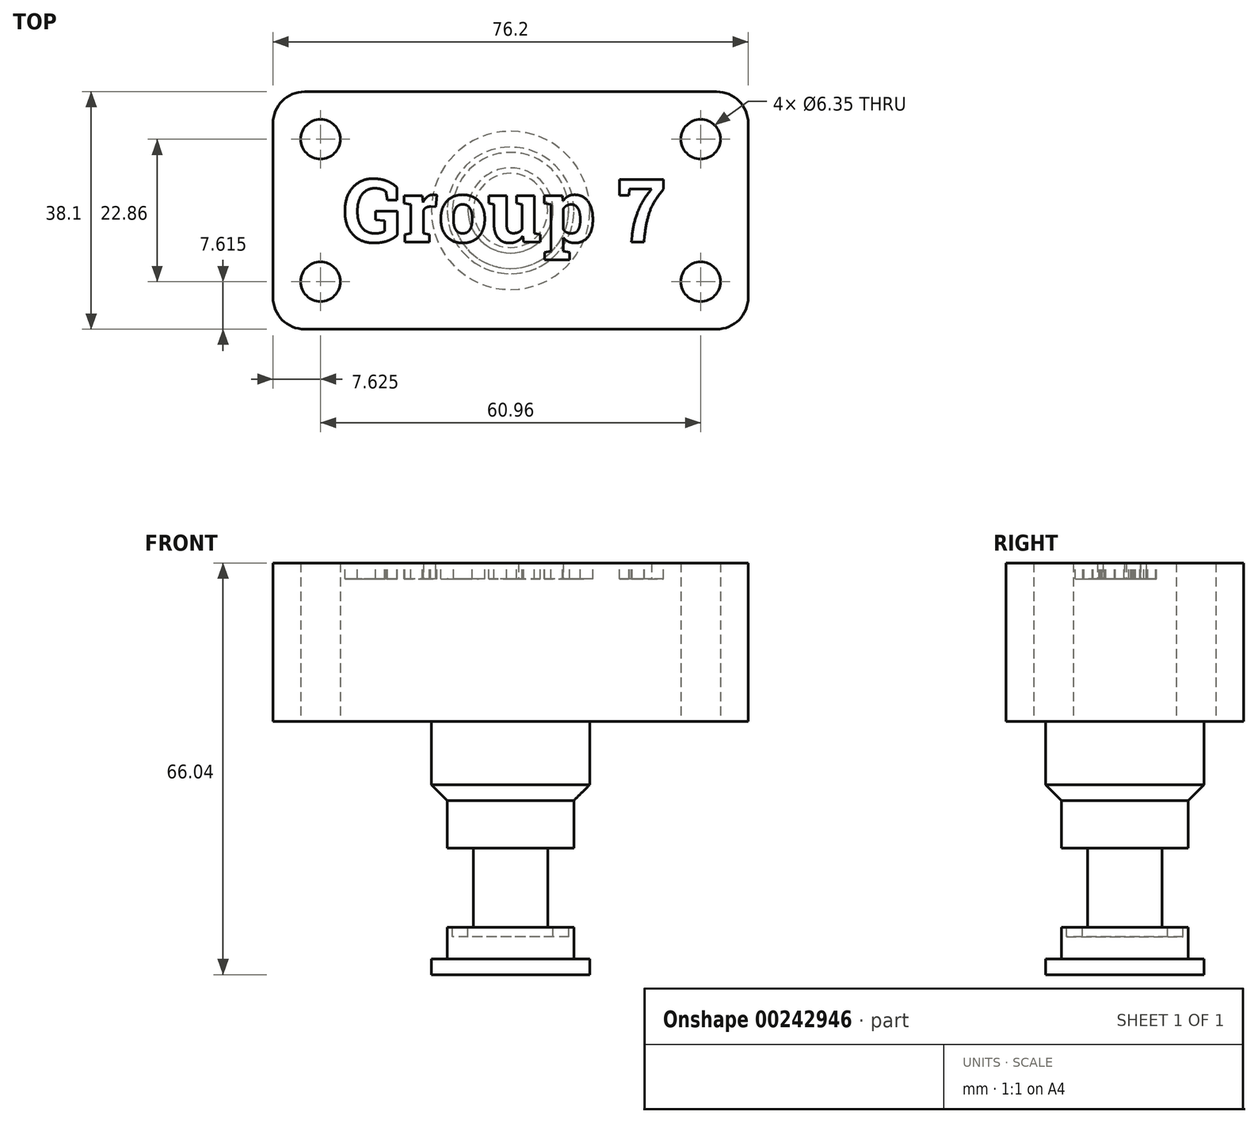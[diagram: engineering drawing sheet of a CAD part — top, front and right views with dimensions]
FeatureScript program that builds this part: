
annotation { "Feature Type Name" : "Feature", "Feature Type Description" : "" }
export const myFeature = defineFeature(function(context is Context, id is Id, definition is map)
    precondition{}
    {
        {
            var Q0;
            Q0=qCreatedBy(makeId("Top.planeOp"),FACE);
            var sketch = newSketch(context, id + "F0", { "sketchPlane" : qUnion([Q0])});
            skLineSegment(sketch, "E0.bottom", {"start": v(-28.39, 17.4) * mm, "end": v(47.81, 17.4) * mm});
            skLineSegment(sketch, "E0.top", {"start": v(-28.39, -20.7) * mm, "end": v(47.81, -20.7) * mm});
            skLineSegment(sketch, "E0.left", {"start": v(-28.39, 17.4) * mm, "end": v(-28.39, -20.7) * mm});
            skLineSegment(sketch, "E0.right", {"start": v(47.81, 17.4) * mm, "end": v(47.81, -20.7) * mm});
            skSolve(sketch);
        }
        {
            var Q0;
            Q0 = qSketchRegion(id + "F0", true);
            extrude(context, id + "F1", {"entities" : qUnion([Q0]), "depth" : 25.4 * mm});
        }
        {
            var Q0;
            Q0=makeQuery(id+"F1.opExtrude","SWEPT_EDGE",EDGE,{"disambiguationData":[OSD([sQuery(id+"F0.wireOp",EDGE,"E0.bottom"),sQuery(id+"F0.wireOp",EDGE,"E0.right")])]});
            var Q1;
            Q1=makeQuery(id+"F1.opExtrude","SWEPT_EDGE",EDGE,{"disambiguationData":[OSD([sQuery(id+"F0.wireOp",EDGE,"E0.top"),sQuery(id+"F0.wireOp",EDGE,"E0.right")])]});
            var Q2;
            Q2=makeQuery(id+"F1.opExtrude","SWEPT_EDGE",EDGE,{"disambiguationData":[OSD([sQuery(id+"F0.wireOp",EDGE,"E0.bottom"),sQuery(id+"F0.wireOp",EDGE,"E0.left")])]});
            var Q3;
            Q3=makeQuery(id+"F1.opExtrude","SWEPT_EDGE",EDGE,{"disambiguationData":[OSD([sQuery(id+"F0.wireOp",EDGE,"E0.top"),sQuery(id+"F0.wireOp",EDGE,"E0.left")])]});
            fillet(context, id + "F2", {"entities" : qUnion([Q0, Q1, Q2, Q3]), "radius" : 5.08 * mm, "tangentPropagation" : true, "allowEdgeOverflow" : false});
        }
        {
            var Q0;
            Q0=qCreatedBy(makeId("Top.planeOp"),FACE);
            var sketch = newSketch(context, id + "F3", { "sketchPlane" : qUnion([Q0])});
            skCircle(sketch, "E1", {"center": v(-20.77, 9.78) * mm, "radius": 3.18 * mm});
            skSolve(sketch);
        }
        {
            var Q0;
            Q0=qCreatedBy(makeId("Top.planeOp"),FACE);
            var sketch = newSketch(context, id + "F4", { "sketchPlane" : qUnion([Q0])});
            skCircle(sketch, "E2", {"center": v(40.2, 9.78) * mm, "radius": 3.18 * mm});
            skSolve(sketch);
        }
        {
            var Q0;
            Q0=qCreatedBy(makeId("Top.planeOp"),FACE);
            var sketch = newSketch(context, id + "F5", { "sketchPlane" : qUnion([Q0])});
            skCircle(sketch, "E3", {"center": v(-20.77, -13.08) * mm, "radius": 3.18 * mm});
            skSolve(sketch);
        }
        {
            var Q0;
            Q0=qCreatedBy(makeId("Top.planeOp"),FACE);
            var sketch = newSketch(context, id + "F6", { "sketchPlane" : qUnion([Q0])});
            skCircle(sketch, "E4", {"center": v(40.2, -13.08) * mm, "radius": 3.18 * mm});
            skSolve(sketch);
        }
        {
            var Q0;
            Q0 = qSketchRegion(id + "F3", true);
            extrude(context, id + "F7", {"entities" : qUnion([Q0]), "operationType" : NewBodyOperationType.REMOVE, "depth" : 25.4 * mm});
        }
        {
            var Q0;
            Q0 = qSketchRegion(id + "F4", true);
            extrude(context, id + "F8", {"entities" : qUnion([Q0]), "operationType" : NewBodyOperationType.REMOVE, "depth" : 25.4 * mm});
        }
        {
            var Q0;
            Q0 = qSketchRegion(id + "F5", true);
            extrude(context, id + "F9", {"entities" : qUnion([Q0]), "operationType" : NewBodyOperationType.REMOVE, "depth" : 25.4 * mm});
        }
        {
            var Q0;
            Q0 = qSketchRegion(id + "F6", true);
            extrude(context, id + "F10", {"entities" : qUnion([Q0]), "operationType" : NewBodyOperationType.REMOVE, "depth" : 25.4 * mm});
        }
        {
            var Q0;
            Q0=qCreatedBy(makeId("Top.planeOp"),FACE);
            var sketch = newSketch(context, id + "F11", { "sketchPlane" : qUnion([Q0])});
            skCircle(sketch, "E5", {"center": v(9.71, -1.65) * mm, "radius": 12.7 * mm});
            skSolve(sketch);
        }
        {
            var Q0;
            Q0 = qSketchRegion(id + "F11", true);
            extrude(context, id + "F12", {"entities" : qUnion([Q0]), "operationType" : NewBodyOperationType.ADD, "oppositeDirection" : true, "depth" : 12.7 * mm});
        }
        {
            var Q0;
            Q0=makeQuery(id+"F12.opExtrude","CAP_EDGE",EDGE,{"disambiguationData":[OSD([sQuery(id+"F11.wireOp",EDGE,"E5")])],"isStart":false});
            chamfer(context, id + "F13", {"entities" : qUnion([Q0]), "width" : 2.54 * mm, "tangentPropagation" : true});
        }
        {
            var Q0;
            Q0=qCreatedBy(makeId("Top.planeOp"),FACE);
            var sketch = newSketch(context, id + "F14", { "sketchPlane" : qUnion([Q0])});
            skCircle(sketch, "E6", {"center": v(9.71, -1.65) * mm, "radius": 10.16 * mm});
            skSolve(sketch);
        }
        {
            var Q0;
            Q0 = qSketchRegion(id + "F14", true);
            extrude(context, id + "F15", {"entities" : qUnion([Q0]), "operationType" : NewBodyOperationType.ADD, "oppositeDirection" : true, "depth" : 38.1 * mm});
        }
        {
            var Q0;
            Q0=makeQuery(id+"F15.opExtrude","CAP_FACE",FACE,{"disambiguationData":[OSD([sQuery(id+"F14.wireOp",EDGE,"E6")])],"isStart":false});
            cPlane(context, id + "F16", {"entities" : qUnion([Q0]), "cplaneType" : CPlaneType.OFFSET, "offset" : 0 * mm, "width" : 152.4 * mm, "height" : 152.4 * mm});
        }
        {
            var Q0;
            Q0=qCreatedBy(id+"F16.planeOp",FACE);
            var sketch = newSketch(context, id + "F17", { "sketchPlane" : qUnion([Q0])});
            skCircle(sketch, "E7", {"center": v(9.71, 1.65) * mm, "radius": 12.7 * mm});
            skSolve(sketch);
        }
        {
            var Q0;
            Q0 = qSketchRegion(id + "F17", true);
            extrude(context, id + "F18", {"entities" : qUnion([Q0]), "operationType" : NewBodyOperationType.ADD, "depth" : 2.54 * mm});
        }
        {
            var Q0;
            Q0=qCreatedBy(makeId("Front.planeOp"),FACE);
            var sketch = newSketch(context, id + "F19", { "sketchPlane" : qUnion([Q0])});
            skLineSegment(sketch, "E8.bottom", {"start": v(-2.35, -20.32) * mm, "end": v(4, -20.32) * mm});
            skLineSegment(sketch, "E8.top", {"start": v(-2.35, -33.02) * mm, "end": v(4, -33.02) * mm});
            skLineSegment(sketch, "E8.left", {"start": v(-2.35, -20.32) * mm, "end": v(-2.35, -33.02) * mm});
            skLineSegment(sketch, "E8.right", {"start": v(4, -20.32) * mm, "end": v(4, -33.02) * mm});
            skSolve(sketch);
        }
        {
            var Q0;
            Q0 = qSketchRegion(id + "F19", true);
            var Q1;
            Q1=makeQuery(id+"F15.opExtrude","SWEPT_FACE",FACE,{"disambiguationData":[OSD([sQuery(id+"F14.wireOp",EDGE,"E6")])]});
            revolve(context, id + "F20", {"operationType" : NewBodyOperationType.REMOVE, "entities" : qUnion([Q0]), "axis" : qUnion([Q1]), "revolveType" : RevolveType.FULL, "oppositeDirection" : true});
        }
        {
            var Q0;
            Q0=qCreatedBy(makeId("Front.planeOp"),FACE);
            var sketch = newSketch(context, id + "F21", { "sketchPlane" : qUnion([Q0])});
            skLineSegment(sketch, "E9.bottom", {"start": v(18.88, -32.03) * mm, "end": v(16.34, -32.03) * mm});
            skLineSegment(sketch, "E9.top", {"start": v(18.88, -34.57) * mm, "end": v(16.34, -34.57) * mm});
            skLineSegment(sketch, "E9.left", {"start": v(18.88, -32.03) * mm, "end": v(18.88, -34.57) * mm});
            skLineSegment(sketch, "E9.right", {"start": v(16.34, -32.03) * mm, "end": v(16.34, -34.57) * mm});
            skSolve(sketch);
        }
        {
            var Q0;
            Q0 = qSketchRegion(id + "F21", true);
            var Q1;
            Q1=makeQuery(id+"F20.boolean.opBoolean","COPY",FACE,{"derivedFrom":makeQuery(id+"F20.opRevolve","SWEPT_FACE",FACE,{"disambiguationData":[OSD([sQuery(id+"F19.wireOp",EDGE,"E8.right")])]})});
            revolve(context, id + "F22", {"operationType" : NewBodyOperationType.REMOVE, "entities" : qUnion([Q0]), "axis" : qUnion([Q1]), "revolveType" : RevolveType.FULL, "oppositeDirection" : true});
        }
        {
            var Q0;
            Q0=makeQuery(id+"F1.opExtrude","CAP_FACE",FACE,{"disambiguationData":[OSD([sQuery(id+"F0.wireOp",EDGE,"E0.bottom"),sQuery(id+"F0.wireOp",EDGE,"E0.top"),sQuery(id+"F0.wireOp",EDGE,"E0.left"),sQuery(id+"F0.wireOp",EDGE,"E0.right")])],"isStart":false});
            var sketch = newSketch(context, id + "F23", { "sketchPlane" : qUnion([Q0])});
            skText(sketch, "E10", { "text": "Group 7", "fontName": "RobotoSlab-Bold.ttf"});
            const initialGuessF23  = {"E10": [-0.01716, -0.00673, 1, 0, 0.01016]};
            skSetInitialGuess(sketch, initialGuessF23);
            skSolve(sketch);
        }
        {
            var Q0;
            Q0 = qSketchRegion(id + "F23", true);
            extrude(context, id + "F24", {"entities" : qUnion([Q0]), "operationType" : NewBodyOperationType.REMOVE, "oppositeDirection" : true, "depth" : 2.54 * mm});
        }
    });
